# Revit family: Plumbing_Drainage_Menzies-Metal_Strainer-Kit-for-Box-Scupper (4)
name_source: partatom
category: Plumbing Fixtures
revit_build: Autodesk Revit 2018 (Build: 20170223_1515(x64)
units: mm (PartAtom-declared; Revit-internal decimal feet)

## family parameters
Cut with Voids When Loaded = No
Host = Face
OmniClass Number = 23.70.50.21.24.11
OmniClass Title = Roof Waste Water Drains
Part Type = Normal
Room Calculation Point = No
Round Connector Dimension = Use Diameter
Shared = Yes

## types (1)
- Strainer Kit for Clamp-TiteBox Scupper
    Assembly Code = D2040200
    Default Elevation = 4' - 0"
    Description = "Strainer Kit for Clamp-Tite Box Scupper"
    Edition number = 1
    Manufacturer = Menzies Metal Products
    Model = 300-3315
    Product Guid = 78de3b7e-1688-4911-bb7a-5cdbd38169c8
    Product Material = Metal - Menzies Metal Products - Mill Aluminum
    Product data url = https://bimobject.com
    URL = https://www.menzies-metal.com
    Weight = 0.60 lbf

## geometry (parser evidence)
native form markers: Sweep x2
no freeform markers — native parametric forms only
